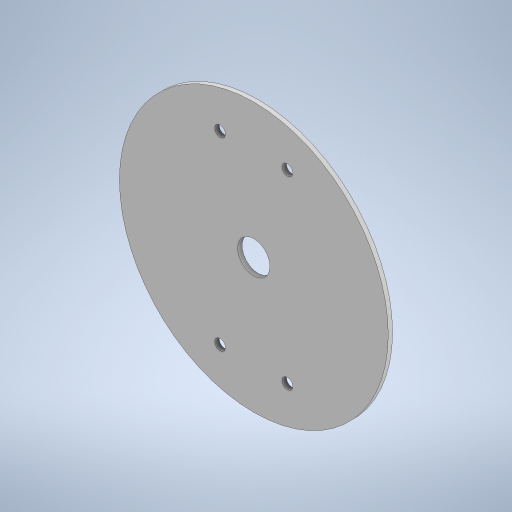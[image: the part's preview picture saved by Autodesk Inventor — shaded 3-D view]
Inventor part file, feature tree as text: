
AUTODESK INVENTOR PART (.ipt)
format: ipt  version: 2023.2 (Build 272271000, 271)  size: 230,912 bytes
history: native  units: mm
features: extrude x1, sketch x1
ambient origin geometry x8: Origin, YZ Plane, XZ Plane, XY Plane, X Axis, Y Axis, Z Axis, Center Point
bodies: Solid1 (feature_tree)
feature tree (2):
  extrude  "Extrusion1"  Depth=4.0mm
  sketch  "Sketch1"  dims[d0=250.0mm d1=30.0mm d2=90.0mm d3=91.5mm d4=91.5mm d6=12.217305mm d8=12.217305mm d9=10.0mm d10=10.0mm d11=4.0mm d12=0.0mm]
